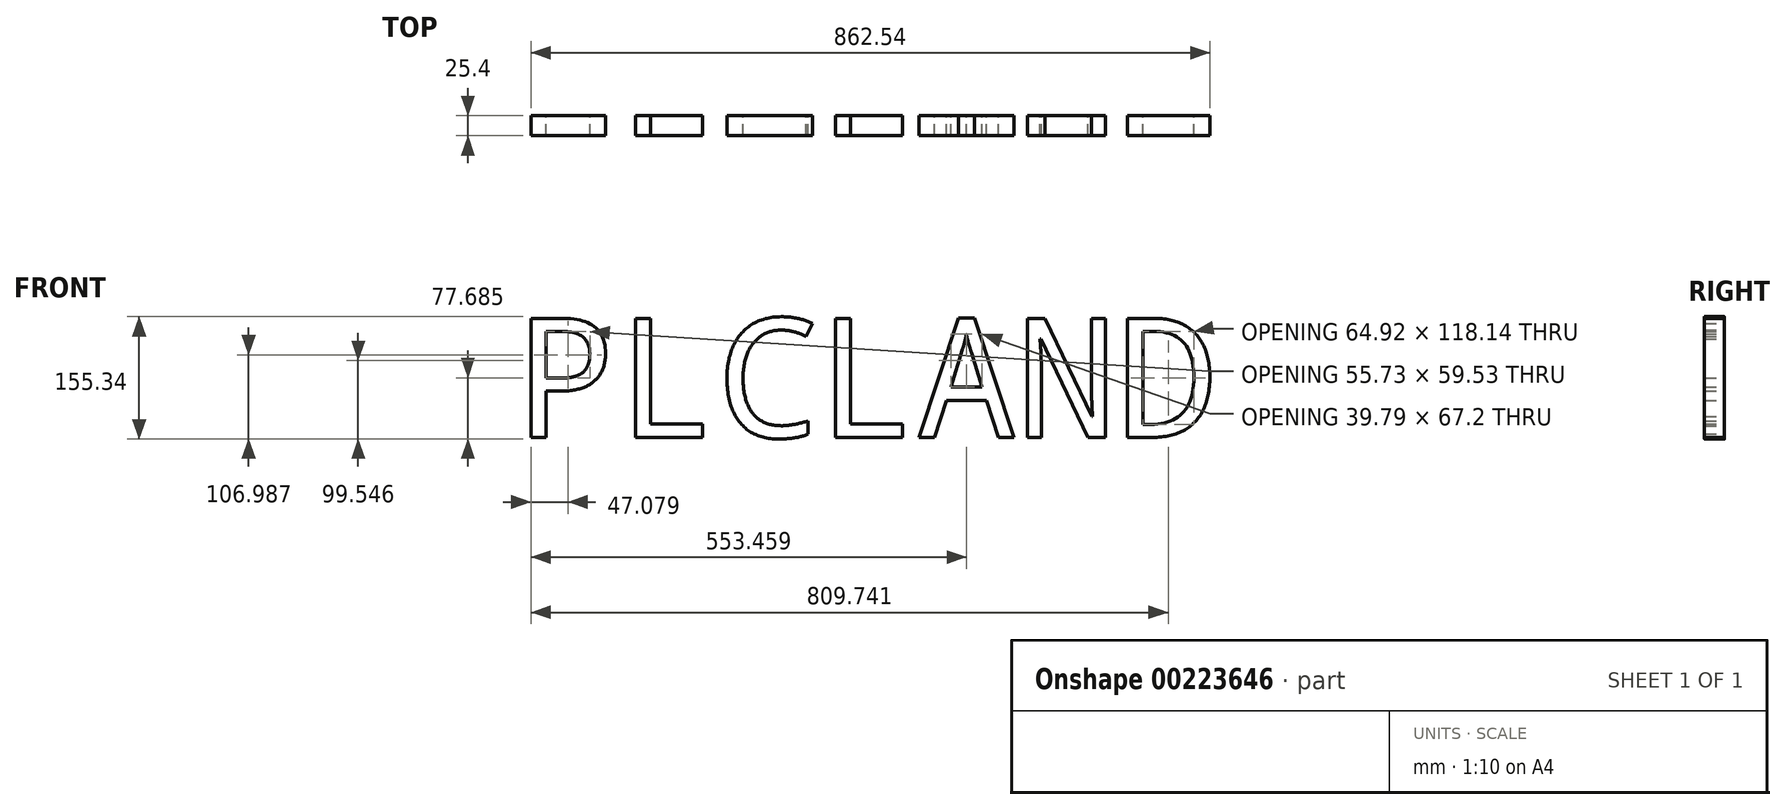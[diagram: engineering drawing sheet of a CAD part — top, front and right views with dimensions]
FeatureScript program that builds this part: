
annotation { "Feature Type Name" : "Feature", "Feature Type Description" : "" }
export const myFeature = defineFeature(function(context is Context, id is Id, definition is map)
    precondition{}
    {
        {
            var Q0;
            Q0=qCreatedBy(makeId("Front.planeOp"),FACE);
            var sketch = newSketch(context, id + "F0", { "sketchPlane" : qUnion([Q0])});
            skText(sketch, "E0", { "text": "PLCLAND", "fontName": "DroidSansMono.ttf"});
            const initialGuessF0  = {"E0": [-0.45624, 0, 1, 0, 0.1524]};
            skSetInitialGuess(sketch, initialGuessF0);
            skSolve(sketch);
        }
        {
            var Q0;
            Q0 = qSketchRegion(id + "F0", true);
            extrude(context, id + "F1", {"entities" : qUnion([Q0]), "depth" : 25.4 * mm});
        }
    });
